# Revit family: Faucet-Flush_Actuator_Sensor-KOHLER-Beam-K-26006T_1
name_source: partatom
category: Plumbing Fixtures
units: mm (PartAtom-declared; Revit-internal decimal feet)

## family parameters
Cut with Voids When Loaded = No
Host = Face
Maintain Annotation Orientation = No
OmniClass Number = 23.31.25.00
OmniClass Title = Toilet and Bath Specialties
Part Type = Normal
Room Calculation Point = No
Round Connector Dimension = Use Diameter
Shared = No

## types (3) — shared parameters
ADA Compliant = No
Assembly Code = D2010
CW Connection = Yes
Cold Water Inlet = Cold Water Inlet
Cold Water Outlet = Cold Water Outlet
Date Modified = 06/28/2022
Default Elevation = 36"
Finish = Kohler-Metal-BN-Vibrant_Brushed_Nickel
Flow Rate = 0 GPM
HW Connection = No
Height = 4 15/16"
Hot Water Inlet = Hot Water Inlet
Length = 3 9/16"
Manufacturer = Kohler Co.
Master Format 2014 = 22 41 39
Master Format 2014 Name = Residential Faucets, Supplies, and Trim
Material = Premium Metal Construction
Pressure = 0.00 psi
Product Name = Beam
URL = http://www.kohler.com.cn
Vent Connection = No
Waste Connection = No
Waste Water Outlet = Waste Water Outlet
WaterSense Certified = No
Width = 4 15/16"

## per-type parameters (varying)
| type | Description | Flush Rate- GPF | Flush Rate- LPF | Model | Type |
| 2.5 LPF, BN-Vibrant Brushed Nickel | PSD URINAL SENSOR, 2.5L | 0.65 GPF | 2.5 LPF | K-26006T-2-BN | 1 |
| 1.0 LPF, BN-Vibrant Brushed Nickel | PSD URINAL SENSOR, 1L | 0.26 GPF | 1 LPF | K-26006T-2W-BN | 2 |
| 0.5 LPF, BN-Vibrant Brushed Nickel | PSD URINAL SENSOR, 0.5L | 0.13 GPF | 0.5 LPF | K-26006T-2Y-BN | 3 |

## geometry (parser evidence)
native form markers: Sweep x4
no freeform markers — native parametric forms only
